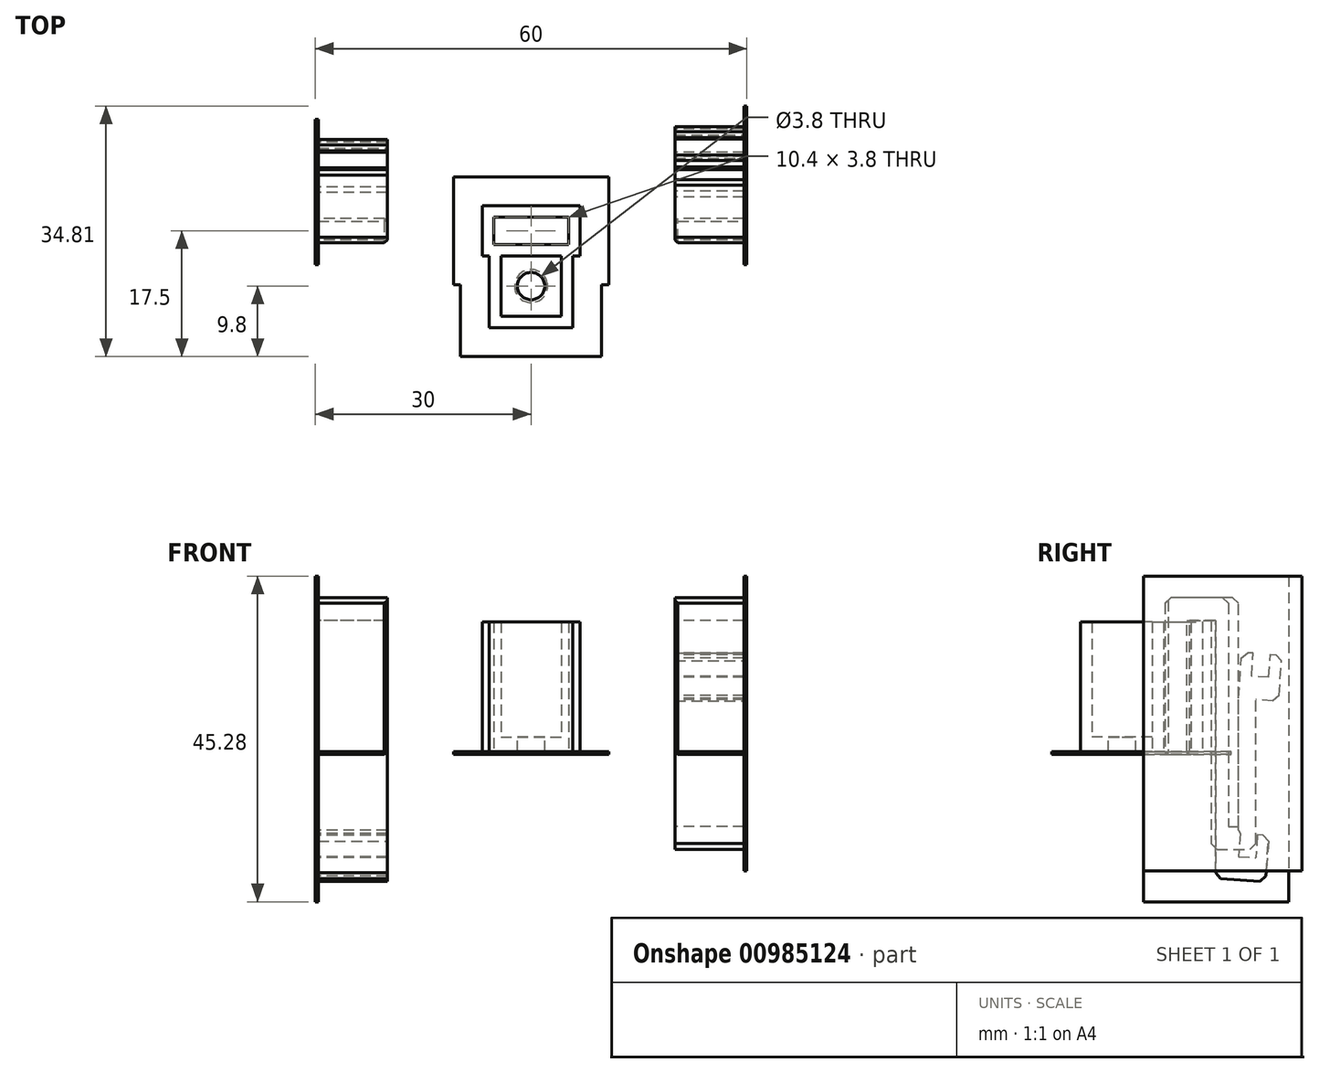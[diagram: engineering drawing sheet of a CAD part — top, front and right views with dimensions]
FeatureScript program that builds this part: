
annotation { "Feature Type Name" : "Feature", "Feature Type Description" : "" }
export const myFeature = defineFeature(function(context is Context, id is Id, definition is map)
    precondition{}
    {
        {
            var Q0;
            Q0=qCreatedBy(makeId("Top.planeOp"),FACE);
            var sketch = newSketch(context, id + "F0", { "sketchPlane" : qUnion([Q0])});
            skLineSegment(sketch, "E0.bottom", {"start": v(-4.2, 4.2) * mm, "end": v(4.2, 4.2) * mm});
            skLineSegment(sketch, "E0.top", {"start": v(-4.2, -4.2) * mm, "end": v(4.2, -4.2) * mm});
            skLineSegment(sketch, "E0.left", {"start": v(-4.2, 4.2) * mm, "end": v(-4.2, -4.2) * mm});
            skLineSegment(sketch, "E0.right", {"start": v(4.2, 4.2) * mm, "end": v(4.2, -4.2) * mm});
            skPoint(sketch, "E0.middle", {"position": v(0, 0) * mm});
            skLineSegment(sketch, "E1.bottom", {"start": v(-5.8, 5.8) * mm, "end": v(5.8, 5.8) * mm});
            skLineSegment(sketch, "E1.top", {"start": v(-5.8, -5.8) * mm, "end": v(5.8, -5.8) * mm});
            skLineSegment(sketch, "E1.left", {"start": v(-5.8, 5.8) * mm, "end": v(-5.8, -5.8) * mm});
            skLineSegment(sketch, "E1.right", {"start": v(5.8, 5.8) * mm, "end": v(5.8, -5.8) * mm});
            skCircle(sketch, "E2", {"center": v(0, 0) * mm, "radius": 1.9 * mm});
            skPoint(sketch, "E3.middle", {"position": v(0, 4.63) * mm});
            skLineSegment(sketch, "E4.bottom", {"start": v(-5.2, 5.8) * mm, "end": v(5.2, 5.8) * mm});
            skLineSegment(sketch, "E4.top", {"start": v(-5.2, 9.6) * mm, "end": v(5.2, 9.6) * mm});
            skLineSegment(sketch, "E4.left", {"start": v(-5.2, 5.8) * mm, "end": v(-5.2, 9.6) * mm});
            skLineSegment(sketch, "E4.right", {"start": v(5.2, 5.8) * mm, "end": v(5.2, 9.6) * mm});
            skPoint(sketch, "E4.middle", {"position": v(0, 7.7) * mm});
            skLineSegment(sketch, "E5.bottom", {"start": v(-6.8, 4.2) * mm, "end": v(6.8, 4.2) * mm});
            skLineSegment(sketch, "E5.top", {"start": v(-6.8, 11.2) * mm, "end": v(6.8, 11.2) * mm});
            skLineSegment(sketch, "E5.left", {"start": v(-6.8, 4.2) * mm, "end": v(-6.8, 11.2) * mm});
            skLineSegment(sketch, "E5.right", {"start": v(6.8, 4.2) * mm, "end": v(6.8, 11.2) * mm});
            skSolve(sketch);
        }
        {
            var Q0;
            Q0=makeQuery(id+"F0.imprint","IMPRINT",FACE,{"disambiguationData":[TD([[makeQuery(id+"F0.imprint","IMPRINT",EDGE,{"derivedFrom":sQuery(id+"F0.wireOp",EDGE,"E0.bottom")}),1.0]])]});
            var Q1;
            Q1=makeQuery(id+"F0.imprint","IMPRINT",FACE,{"disambiguationData":[TD([[makeQuery(id+"F0.imprint","IMPRINT",EDGE,{"derivedFrom":sQuery(id+"F0.wireOp",EDGE,"E0.top")}),-1.0]])]});
            var Q2;
            {var subQ9=sQuery(id+"F0.wireOp",EDGE,"E4.bottom");Q2=makeQuery(id+"F0.imprint","IMPRINT",FACE,{"disambiguationData":[TD([[makeQuery(id+"F0.imprint","IMPRINT",EDGE,{"derivedFrom":subQ9}),-1.0]])]});}
            var Q3;
            Q3=makeQuery(id+"F0.imprint","IMPRINT",FACE,{"disambiguationData":[TD([[makeQuery(id+"F0.imprint","IMPRINT",EDGE,{"derivedFrom":sQuery(id+"F0.wireOp",EDGE,"E4.top")}),1.0]])]});
            var Q4;
            {var subQ0=sQuery(id+"F0.wireOp",EDGE,"E4.bottom");var subQ1=sQuery(id+"F0.wireOp",EDGE,"E1.left");var subQ2=makeQuery(id+"F0.imprint","INTERSECT",VERTEX,{"derivedFrom":[subQ1,subQ0]});Q4=makeQuery(id+"F0.imprint","IMPRINT",FACE,{"disambiguationData":[TD([[makeQuery(id+"F0.imprint","IMPRINT",EDGE,{"disambiguationData":[TD([[subQ2,-1.0]])],"derivedFrom":subQ1}),1.0]])]});}
            extrude(context, id + "F1", {"entities" : qUnion([Q0, Q1, Q2, Q3, Q4]), "depth" : 16 * mm, "offsetDistance" : 25 * mm});
        }
        {
            var Q0;
            Q0=makeQuery(id+"F0.imprint","IMPRINT",FACE,{"disambiguationData":[TD([[makeQuery(id+"F0.imprint","IMPRINT",EDGE,{"derivedFrom":sQuery(id+"F0.wireOp",EDGE,"AogjtpNg-7Dl6-KLo7-kLo7-PgsWRjaplvz6.bottom")}),1.0]])]});
            var Q1;
            Q1=makeQuery(id+"F0.imprint","IMPRINT",FACE,{"disambiguationData":[TD([[makeQuery(id+"F0.imprint","IMPRINT",EDGE,{"derivedFrom":sQuery(id+"F0.wireOp",EDGE,"E0.bottom")}),1.0]])]});
            var Q2;
            Q2=makeQuery(id+"F0.imprint","IMPRINT",FACE,{"disambiguationData":[TD([[makeQuery(id+"F0.imprint","IMPRINT",EDGE,{"derivedFrom":sQuery(id+"F0.wireOp",EDGE,"E0.bottom")}),-1.0]])]});
            var Q3;
            Q3=makeQuery(id+"F0.imprint","IMPRINT",FACE,{"disambiguationData":[TD([[makeQuery(id+"F0.imprint","IMPRINT",EDGE,{"derivedFrom":sQuery(id+"F0.wireOp",EDGE,"lpZYiEbC-BTsA-Mxmd-cXDk-FG9kW4EGSvv5.bottom")}),-1.0]])]});
            var Q4;
            Q4=makeQuery(id+"F0.imprint","IMPRINT",FACE,{"disambiguationData":[TD([[makeQuery(id+"F0.imprint","IMPRINT",EDGE,{"derivedFrom":sQuery(id+"F0.wireOp",EDGE,"fRjwv1VZ-xKsu-zfrT-GSA2-1ylmCSNZtOP4.bottom")}),1.0]])]});
            var Q5;
            {var subQ9=sQuery(id+"F0.wireOp",EDGE,"AogjtpNg-7Dl6-KLo7-kLo7-PgsWRjaplvz6.top");Q5=makeQuery(id+"F0.imprint","IMPRINT",FACE,{"disambiguationData":[TD([[makeQuery(id+"F0.imprint","IMPRINT",EDGE,{"derivedFrom":subQ9}),-1.0]])]});}
            var Q6;
            Q6=makeQuery(id+"F0.imprint","IMPRINT",FACE,{"disambiguationData":[TD([[makeQuery(id+"F0.imprint","IMPRINT",EDGE,{"derivedFrom":sQuery(id+"F0.wireOp",EDGE,"E4.top")}),1.0]])]});
            var Q7;
            Q7=makeQuery(id+"F0.imprint","IMPRINT",FACE,{"disambiguationData":[TD([[makeQuery(id+"F0.imprint","IMPRINT",EDGE,{"derivedFrom":sQuery(id+"F0.wireOp",EDGE,"E0.top")}),-1.0]])]});
            var Q8;
            {var subQ9=sQuery(id+"F0.wireOp",EDGE,"E4.bottom");Q8=makeQuery(id+"F0.imprint","IMPRINT",FACE,{"disambiguationData":[TD([[makeQuery(id+"F0.imprint","IMPRINT",EDGE,{"derivedFrom":subQ9}),-1.0]])]});}
            var Q9;
            Q9=makeQuery(id+"F0.imprint","IMPRINT",FACE,{"disambiguationData":[TD([[makeQuery(id+"F0.imprint","IMPRINT",EDGE,{"derivedFrom":sQuery(id+"F0.wireOp",EDGE,"E0.top")}),1.0]])]});
            var Q10;
            {var subQ0=sQuery(id+"F0.wireOp",EDGE,"E4.bottom");var subQ1=sQuery(id+"F0.wireOp",EDGE,"E1.left");var subQ2=makeQuery(id+"F0.imprint","INTERSECT",VERTEX,{"derivedFrom":[subQ1,subQ0]});Q10=makeQuery(id+"F0.imprint","IMPRINT",FACE,{"disambiguationData":[TD([[makeQuery(id+"F0.imprint","IMPRINT",EDGE,{"disambiguationData":[TD([[subQ2,-1.0]])],"derivedFrom":subQ1}),1.0]])]});}
            extrude(context, id + "F2", {"entities" : qUnion([Q0, Q1, Q2, Q3, Q4, Q5, Q6, Q7, Q8, Q9, Q10]), "operationType" : NewBodyOperationType.ADD, "oppositeDirection" : true, "depth" : 2.4 * mm, "offsetDistance" : 25 * mm});
        }
        {
            var Q0;
            Q0=qCreatedBy(makeId("Right.planeOp"),FACE);
            cPlane(context, id + "F3", {"entities" : qUnion([Q0]), "cplaneType" : CPlaneType.OFFSET, "offset" : 25 * mm, "oppositeDirection" : true, "width" : 150 * mm, "height" : 150 * mm});
        }
        {
            var Q0;
            Q0=qCreatedBy(id+"F3.planeOp",FACE);
            var sketch = newSketch(context, id + "F4", { "sketchPlane" : qUnion([Q0])});
            skPoint(sketch, "E6.0", {"position": v(9.6, -2.4) * mm});
            skPoint(sketch, "E6.1", {"position": v(5.8, -2.4) * mm});
            skPoint(sketch, "E6.2", {"position": v(9.6, 16) * mm});
            skPoint(sketch, "E6.3", {"position": v(5.8, 16) * mm});
            skLineSegment(sketch, "E7.bottom", {"start": v(9.6, -2.4) * mm, "end": v(5.8, -2.4) * mm, "construction": true});
            skLineSegment(sketch, "E7.top", {"start": v(9.6, 16) * mm, "end": v(5.8, 16) * mm, "construction": true});
            skLineSegment(sketch, "E7.left", {"start": v(9.6, -2.4) * mm, "end": v(9.6, 16) * mm, "construction": true});
            skLineSegment(sketch, "E7.right", {"start": v(5.8, -2.4) * mm, "end": v(5.8, 16) * mm, "construction": true});
            skLineSegment(sketch, "E8.bottom", {"start": v(6, -2.4) * mm, "end": v(9.4, -2.4) * mm});
            skLineSegment(sketch, "E8.top", {"start": v(6, 19.4) * mm, "end": v(9.4, 19.4) * mm});
            skLineSegment(sketch, "E8.left", {"start": v(6, -2.4) * mm, "end": v(6, 19.4) * mm});
            skLineSegment(sketch, "E8.right", {"start": v(9.4, -2.4) * mm, "end": v(9.4, 19.4) * mm});
            skLineSegment(sketch, "E9.bottom", {"start": v(9.4, 19.4) * mm, "end": v(13, 19.4) * mm});
            skLineSegment(sketch, "E9.top", {"start": v(9.4, 16.2) * mm, "end": v(13, 16.2) * mm});
            skLineSegment(sketch, "E9.left", {"start": v(9.4, 19.4) * mm, "end": v(9.4, 16.2) * mm});
            skLineSegment(sketch, "E9.right", {"start": v(13, 19.4) * mm, "end": v(13, 16.2) * mm});
            skLineSegment(sketch, "E10.bottom", {"start": v(13, 19.4) * mm, "end": v(16.2, 19.4) * mm});
            skLineSegment(sketch, "E10.top", {"start": v(13, -16.6) * mm, "end": v(16.2, -16.6) * mm});
            skLineSegment(sketch, "E10.left", {"start": v(13, 19.4) * mm, "end": v(13, -16.6) * mm});
            skLineSegment(sketch, "E10.right", {"start": v(16.2, 19.4) * mm, "end": v(16.2, -16.6) * mm});
            skLineSegment(sketch, "E11.bottom", {"start": v(19.97, -20.07) * mm, "end": v(14.38, -19.68) * mm});
            skLineSegment(sketch, "E11.left", {"start": v(19.97, -20.07) * mm, "end": v(20.41, -13.69) * mm});
            skLineSegment(sketch, "E11.right", {"start": v(14.38, -19.68) * mm, "end": v(14.83, -13.3) * mm});
            skLineSegment(sketch, "E12.bottom", {"start": v(18.6, -16.77) * mm, "end": v(16.2, -16.6) * mm});
            skLineSegment(sketch, "E12.left", {"start": v(18.6, -16.77) * mm, "end": v(18.82, -13.58) * mm});
            skLineSegment(sketch, "E12.right", {"start": v(16.2, -16.6) * mm, "end": v(16.42, -13.4) * mm});
            skLineSegment(sketch, "E13", {"start": v(18.82, -13.58) * mm, "end": v(20.41, -13.69) * mm});
            skLineSegment(sketch, "E14", {"start": v(16.42, -13.4) * mm, "end": v(14.83, -13.3) * mm});
            skLineSegment(sketch, "E15", {"start": v(13, -16.6) * mm, "end": v(14.38, -19.68) * mm});
            skLineSegment(sketch, "E16", {"start": v(16.42, -13.4) * mm, "end": v(16.2, -12.9) * mm});
            skLineSegment(sketch, "E17", {"start": v(13, -16.6) * mm, "end": v(13, -19.58) * mm});
            skLineSegment(sketch, "E18", {"start": v(13, -19.58) * mm, "end": v(14.38, -19.68) * mm});
            skSolve(sketch);
        }
        {
            var Q0;
            Q0=makeQuery(id+"F4.imprint","IMPRINT",FACE,{"disambiguationData":[TD([[makeQuery(id+"F4.imprint","IMPRINT",EDGE,{"derivedFrom":sQuery(id+"F4.wireOp",EDGE,"E8.bottom")}),1.0]])]});
            var Q1;
            {var subQ3=sQuery(id+"F4.wireOp",EDGE,"E10.bottom");Q1=makeQuery(id+"F4.imprint","IMPRINT",FACE,{"disambiguationData":[TD([[makeQuery(id+"F4.imprint","IMPRINT",EDGE,{"derivedFrom":subQ3}),-1.0]])]});}
            var Q2;
            {var subQ0=sQuery(id+"F4.wireOp",EDGE,"E9.bottom");Q2=makeQuery(id+"F4.imprint","IMPRINT",FACE,{"disambiguationData":[TD([[makeQuery(id+"F4.imprint","IMPRINT",EDGE,{"derivedFrom":subQ0}),-1.0]])]});}
            var Q3;
            {var subQ3=sQuery(id+"F4.wireOp",EDGE,"E11.right");var subQ5=sQuery(id+"F4.wireOp",EDGE,"E14");var subQ7=makeQuery(id+"F4.imprint","INTERSECT",VERTEX,{"derivedFrom":[subQ3,subQ5]});Q3=makeQuery(id+"F4.imprint","IMPRINT",FACE,{"disambiguationData":[TD([[makeQuery(id+"F4.imprint","IMPRINT",EDGE,{"disambiguationData":[TD([[subQ7,1.0]])],"derivedFrom":subQ3}),-1.0]])]});}
            var Q4;
            {var subQ1=sQuery(id+"F4.wireOp",EDGE,"E11.bottom");Q4=makeQuery(id+"F4.imprint","IMPRINT",FACE,{"disambiguationData":[TD([[makeQuery(id+"F4.imprint","IMPRINT",EDGE,{"derivedFrom":subQ1}),-1.0]])]});}
            var Q5;
            {var subQ0=sQuery(id+"F4.wireOp",EDGE,"E15");Q5=makeQuery(id+"F4.imprint","IMPRINT",FACE,{"disambiguationData":[TD([[makeQuery(id+"F4.imprint","IMPRINT",EDGE,{"derivedFrom":subQ0}),1.0]])]});}
            var Q6;
            {var subQ0=sQuery(id+"F4.wireOp",EDGE,"E12.right");Q6=makeQuery(id+"F4.imprint","IMPRINT",FACE,{"disambiguationData":[TD([[makeQuery(id+"F4.imprint","IMPRINT",EDGE,{"derivedFrom":subQ0}),1.0]])]});}
            var Q7;
            {var subQ0=sQuery(id+"F4.wireOp",EDGE,"E16");Q7=makeQuery(id+"F4.imprint","IMPRINT",FACE,{"disambiguationData":[TD([[makeQuery(id+"F4.imprint","IMPRINT",EDGE,{"derivedFrom":subQ0}),1.0]])]});}
            var Q8;
            Q8=makeQuery(id+"F4.imprint","IMPRINT",FACE,{"disambiguationData":[TD([[makeQuery(id+"F4.imprint","IMPRINT",EDGE,{"derivedFrom":sQuery(id+"F4.wireOp",EDGE,"E15")}),-1.0]])]});
            extrude(context, id + "F5", {"entities" : qUnion([Q0, Q1, Q2, Q3, Q4, Q5, Q6, Q7, Q8]), "depth" : 10 * mm, "offsetDistance" : 25 * mm, "symmetric" : true});
        }
        {
            var Q0;
            Q0=makeQuery(id+"F5.opExtrude","SWEPT_EDGE",EDGE,{"disambiguationData":[OSD([sQuery(id+"F4.wireOp",EDGE,"E11.bottom"),sQuery(id+"F4.wireOp",EDGE,"E11.left")])]});
            var Q1;
            Q1=makeQuery(id+"F5.opExtrude","SWEPT_EDGE",EDGE,{"disambiguationData":[OSD([sQuery(id+"F4.wireOp",EDGE,"E11.left"),sQuery(id+"F4.wireOp",EDGE,"E13")])]});
            var Q2;
            Q2=makeQuery(id+"F5.opExtrude","SWEPT_EDGE",EDGE,{"disambiguationData":[OSD([sQuery(id+"F4.wireOp",EDGE,"E11.bottom"),sQuery(id+"F4.wireOp",EDGE,"E11.right"),sQuery(id+"F4.wireOp",EDGE,"E15")])]});
            var Q3;
            Q3=makeQuery(id+"F5.opExtrude","SWEPT_EDGE",EDGE,{"disambiguationData":[OSD([sQuery(id+"F4.wireOp",EDGE,"E10.bottom"),sQuery(id+"F4.wireOp",EDGE,"E10.right")])]});
            var Q4;
            Q4=makeQuery(id+"F5.opExtrude","SWEPT_EDGE",EDGE,{"disambiguationData":[OSD([sQuery(id+"F4.wireOp",EDGE,"E8.top"),sQuery(id+"F4.wireOp",EDGE,"E8.left")])]});
            var Q5;
            Q5=makeQuery(id+"F5.opExtrude","SWEPT_EDGE",EDGE,{"disambiguationData":[OSD([sQuery(id+"F4.wireOp",EDGE,"E17"),sQuery(id+"F4.wireOp",EDGE,"E18")])]});
            chamfer(context, id + "F6", {"entities" : qUnion([Q0, Q1, Q2, Q3, Q4, Q5]), "width" : 0.8 * mm, "tangentPropagation" : true});
        }
        {
            var Q0;
            Q0=qCreatedBy(makeId("Right.planeOp"),FACE);
            cPlane(context, id + "F7", {"entities" : qUnion([Q0]), "cplaneType" : CPlaneType.OFFSET, "offset" : 25 * mm, "width" : 150 * mm, "height" : 150 * mm});
        }
        {
            var Q0;
            Q0=qCreatedBy(id+"F7.planeOp",FACE);
            var sketch = newSketch(context, id + "F8", { "sketchPlane" : qUnion([Q0])});
            skPoint(sketch, "E19.0", {"position": v(9.6, -2.4) * mm});
            skPoint(sketch, "E19.1", {"position": v(5.8, -2.4) * mm});
            skPoint(sketch, "E19.2", {"position": v(5.8, 16) * mm});
            skPoint(sketch, "E19.3", {"position": v(9.6, 16) * mm});
            skLineSegment(sketch, "E20.bottom", {"start": v(5.8, 16) * mm, "end": v(9.6, 16) * mm, "construction": true});
            skLineSegment(sketch, "E20.top", {"start": v(5.8, -2.4) * mm, "end": v(9.6, -2.4) * mm, "construction": true});
            skLineSegment(sketch, "E20.left", {"start": v(5.8, 16) * mm, "end": v(5.8, -2.4) * mm, "construction": true});
            skLineSegment(sketch, "E20.right", {"start": v(9.6, 16) * mm, "end": v(9.6, -2.4) * mm, "construction": true});
            skPoint(sketch, "E21.0", {"position": v(9.4, 19.4) * mm});
            skPoint(sketch, "E21.1", {"position": v(6, 19.4) * mm});
            skPoint(sketch, "E21.2", {"position": v(9.4, -2.4) * mm});
            skPoint(sketch, "E21.3", {"position": v(6, -2.4) * mm});
            skLineSegment(sketch, "E22.bottom", {"start": v(9.4, 19.4) * mm, "end": v(6, 19.4) * mm});
            skLineSegment(sketch, "E22.top", {"start": v(9.4, -2.4) * mm, "end": v(6, -2.4) * mm});
            skLineSegment(sketch, "E22.left", {"start": v(9.4, 19.4) * mm, "end": v(9.4, -2.4) * mm});
            skLineSegment(sketch, "E22.right", {"start": v(6, 19.4) * mm, "end": v(6, -2.4) * mm});
            skPoint(sketch, "E23.0", {"position": v(9.4, 16.2) * mm});
            skLineSegment(sketch, "E24.bottom", {"start": v(9.4, 19.4) * mm, "end": v(9.4, 19.4) * mm});
            skLineSegment(sketch, "E24.top", {"start": v(9.4, 16.2) * mm, "end": v(9.4, 16.2) * mm});
            skLineSegment(sketch, "E24.left", {"start": v(9.4, 19.4) * mm, "end": v(9.4, 16.2) * mm});
            skLineSegment(sketch, "E24.right", {"start": v(9.4, 19.4) * mm, "end": v(9.4, 16.2) * mm});
            skLineSegment(sketch, "E25.bottom", {"start": v(9.4, 19.4) * mm, "end": v(12.4, 19.4) * mm});
            skLineSegment(sketch, "E25.top", {"start": v(9.4, 16.2) * mm, "end": v(12.4, 16.2) * mm});
            skLineSegment(sketch, "E25.right", {"start": v(12.4, 19.4) * mm, "end": v(12.4, 16.2) * mm});
            skLineSegment(sketch, "E26.0", {"start": v(16.2, 5.4) * mm, "end": v(16.65, 11.78) * mm});
            skLineSegment(sketch, "E26.1", {"start": v(18.02, 8.48) * mm, "end": v(18.24, 11.67) * mm});
            skLineSegment(sketch, "E26.2", {"start": v(20.41, 8.31) * mm, "end": v(20.64, 11.5) * mm});
            skLineSegment(sketch, "E26.3", {"start": v(21.79, 5) * mm, "end": v(22.23, 11.4) * mm});
            skLineSegment(sketch, "E26.4", {"start": v(20.64, 11.5) * mm, "end": v(22.23, 11.4) * mm});
            skLineSegment(sketch, "E26.5", {"start": v(21.79, 5) * mm, "end": v(16.2, 5.4) * mm});
            skLineSegment(sketch, "E26.6", {"start": v(18.24, 11.67) * mm, "end": v(16.65, 11.78) * mm});
            skLineSegment(sketch, "E26.7", {"start": v(20.41, 8.31) * mm, "end": v(18.02, 8.48) * mm});
            skLineSegment(sketch, "E27.bottom", {"start": v(12.4, 19.4) * mm, "end": v(14.8, 19.4) * mm});
            skLineSegment(sketch, "E27.top", {"start": v(12.4, -15.6) * mm, "end": v(14.8, -15.6) * mm});
            skLineSegment(sketch, "E27.left", {"start": v(12.4, 19.4) * mm, "end": v(12.4, -15.6) * mm});
            skLineSegment(sketch, "E27.right", {"start": v(14.8, 19.4) * mm, "end": v(14.8, -15.6) * mm});
            skLineSegment(sketch, "E28.bottom", {"start": v(14.8, -15.6) * mm, "end": v(16.2, -15.6) * mm});
            skLineSegment(sketch, "E28.top", {"start": v(14.8, -12.4) * mm, "end": v(16.2, -12.4) * mm});
            skLineSegment(sketch, "E28.left", {"start": v(14.8, -15.6) * mm, "end": v(14.8, -12.4) * mm});
            skLineSegment(sketch, "E28.right", {"start": v(16.2, -15.6) * mm, "end": v(16.2, -12.4) * mm});
            skLineSegment(sketch, "E29.bottom", {"start": v(16.2, -15.6) * mm, "end": v(18.6, -15.6) * mm});
            skLineSegment(sketch, "E29.top", {"start": v(16.2, 5.4) * mm, "end": v(18.6, 5.4) * mm});
            skLineSegment(sketch, "E29.left", {"start": v(16.2, -15.6) * mm, "end": v(16.2, 5.4) * mm});
            skLineSegment(sketch, "E29.right", {"start": v(18.6, -15.6) * mm, "end": v(18.6, 5.4) * mm});
            skSolve(sketch);
        }
        {
            var Q0;
            Q0=qSketchRegion(id+"F8",true);
            extrude(context, id + "F9", {"entities" : qUnion([Q0]), "depth" : 10 * mm, "offsetDistance" : 25 * mm, "symmetric" : true});
        }
        {
            var Q0;
            Q0=makeQuery(id+"F9.opExtrude","SWEPT_EDGE",EDGE,{"disambiguationData":[OSD([sQuery(id+"F8.wireOp",EDGE,"E26.3"),sQuery(id+"F8.wireOp",EDGE,"E26.4")])]});
            var Q1;
            Q1=makeQuery(id+"F9.opExtrude","SWEPT_EDGE",EDGE,{"disambiguationData":[OSD([sQuery(id+"F8.wireOp",EDGE,"E26.3"),sQuery(id+"F8.wireOp",EDGE,"E26.5")])]});
            var Q2;
            Q2=makeQuery(id+"F9.opExtrude","SWEPT_EDGE",EDGE,{"disambiguationData":[OSD([sQuery(id+"F8.wireOp",EDGE,"gtvTyELX-qYsY-zlD4-YZin-kNKeZDM44uR5.bottom"),sQuery(id+"F8.wireOp",EDGE,"gtvTyELX-qYsY-zlD4-YZin-kNKeZDM44uR5.right")])]});
            var Q3;
            Q3=makeQuery(id+"F9.opExtrude","SWEPT_EDGE",EDGE,{"disambiguationData":[OSD([sQuery(id+"F8.wireOp",EDGE,"pzn4xJtv-Sc2h-J7Oc-zair-ZdfKoGXIpqRY.top"),sQuery(id+"F8.wireOp",EDGE,"pzn4xJtv-Sc2h-J7Oc-zair-ZdfKoGXIpqRY.left")])]});
            var Q4;
            Q4=makeQuery(id+"F9.opExtrude","SWEPT_EDGE",EDGE,{"disambiguationData":[OSD([sQuery(id+"F8.wireOp",EDGE,"E26.0"),sQuery(id+"F8.wireOp",EDGE,"E26.6"),sQuery(id+"F8.wireOp",EDGE,"qTeprqho-zbRK-rMkQ-vlma-PGJ56aoAsNja")])]});
            var Q5;
            Q5=makeQuery(id+"F9.opExtrude","SWEPT_EDGE",EDGE,{"disambiguationData":[OSD([sQuery(id+"F8.wireOp",EDGE,"pzn4xJtv-Sc2h-J7Oc-zair-ZdfKoGXIpqRY.bottom"),sQuery(id+"F8.wireOp",EDGE,"pzn4xJtv-Sc2h-J7Oc-zair-ZdfKoGXIpqRY.right")])]});
            var Q6;
            Q6=makeQuery(id+"F9.opExtrude","SWEPT_EDGE",EDGE,{"disambiguationData":[OSD([sQuery(id+"F8.wireOp",EDGE,"E22.bottom"),sQuery(id+"F8.wireOp",EDGE,"E22.right")])]});
            var Q7;
            Q7=makeQuery(id+"F9.opExtrude","SWEPT_EDGE",EDGE,{"disambiguationData":[OSD([sQuery(id+"F8.wireOp",EDGE,"E27.bottom"),sQuery(id+"F8.wireOp",EDGE,"E27.right")])]});
            var Q8;
            Q8=makeQuery(id+"F9.opExtrude","SWEPT_EDGE",EDGE,{"disambiguationData":[OSD([sQuery(id+"F8.wireOp",EDGE,"E29.bottom"),sQuery(id+"F8.wireOp",EDGE,"E29.right")])]});
            var Q9;
            Q9=makeQuery(id+"F9.opExtrude","SWEPT_EDGE",EDGE,{"disambiguationData":[OSD([sQuery(id+"F8.wireOp",EDGE,"E27.top"),sQuery(id+"F8.wireOp",EDGE,"E27.left")])]});
            chamfer(context, id + "F10", {"entities" : qUnion([Q0, Q1, Q2, Q3, Q4, Q5, Q6, Q7, Q8, Q9]), "width" : 0.8 * mm, "tangentPropagation" : true});
        }
        {
            var Q0;
            Q0=makeQuery(id+"F2.opExtrude","CAP_FACE",FACE,{"disambiguationData":[OSD([sQuery(id+"F0.wireOp",EDGE,"E1.top"),sQuery(id+"F0.wireOp",EDGE,"E1.left"),sQuery(id+"F0.wireOp",EDGE,"E1.right"),sQuery(id+"F0.wireOp",EDGE,"E2"),sQuery(id+"F0.wireOp",EDGE,"E4.bottom"),sQuery(id+"F0.wireOp",EDGE,"E4.top"),sQuery(id+"F0.wireOp",EDGE,"E4.left"),sQuery(id+"F0.wireOp",EDGE,"E4.right"),sQuery(id+"F0.wireOp",EDGE,"E5.bottom"),sQuery(id+"F0.wireOp",EDGE,"E5.top"),sQuery(id+"F0.wireOp",EDGE,"E5.left"),sQuery(id+"F0.wireOp",EDGE,"E5.right")])],"isStart":false});
            var sketch = newSketch(context, id + "F11", { "sketchPlane" : qUnion([Q0])});
            skSolve(sketch);
        }
        {
            var Q0;
            Q0=makeQuery(id+"F9.opExtrude","CAP_EDGE",EDGE,{"disambiguationData":[OSD([sQuery(id+"F8.wireOp",EDGE,"E22.right")])],"isStart":false});
            var Q1;
            Q1=makeQuery(id+"F9.opExtrude","CAP_EDGE",EDGE,{"disambiguationData":[OSD([sQuery(id+"F8.wireOp",EDGE,"E22.left")])],"isStart":false});
            var Q2;
            Q2=makeQuery(id+"F9.opExtrude","CAP_EDGE",EDGE,{"disambiguationData":[OSD([sQuery(id+"F8.wireOp",EDGE,"E22.right")])],"isStart":true});
            var Q3;
            Q3=makeQuery(id+"F9.opExtrude","SWEPT_EDGE",EDGE,{"disambiguationData":[OSD([sQuery(id+"F8.wireOp",EDGE,"E22.top"),sQuery(id+"F8.wireOp",EDGE,"E22.right")])]});
            var Q4;
            Q4=makeQuery(id+"F9.opExtrude","CAP_EDGE",EDGE,{"disambiguationData":[OSD([sQuery(id+"F8.wireOp",EDGE,"E22.top")])],"isStart":true});
            var Q5;
            Q5=makeQuery(id+"F9.opExtrude","SWEPT_EDGE",EDGE,{"disambiguationData":[OSD([sQuery(id+"F8.wireOp",EDGE,"E22.top"),sQuery(id+"F8.wireOp",EDGE,"E22.left")])]});
            var Q6;
            Q6=makeQuery(id+"F9.opExtrude","CAP_EDGE",EDGE,{"disambiguationData":[OSD([sQuery(id+"F8.wireOp",EDGE,"E22.top")])],"isStart":false});
            var Q7;
            Q7=makeQuery(id+"F9.opExtrude","CAP_EDGE",EDGE,{"disambiguationData":[OSD([sQuery(id+"F8.wireOp",EDGE,"E22.left")])],"isStart":true});
            var Q8;
            Q8=makeQuery(id+"F5.opExtrude","CAP_EDGE",EDGE,{"disambiguationData":[OSD([sQuery(id+"F4.wireOp",EDGE,"E8.bottom")])],"isStart":true});
            var Q9;
            Q9=makeQuery(id+"F5.opExtrude","SWEPT_EDGE",EDGE,{"disambiguationData":[OSD([sQuery(id+"F4.wireOp",EDGE,"E8.bottom"),sQuery(id+"F4.wireOp",EDGE,"E8.left")])]});
            var Q10;
            Q10=makeQuery(id+"F5.opExtrude","CAP_EDGE",EDGE,{"disambiguationData":[OSD([sQuery(id+"F4.wireOp",EDGE,"E8.bottom")])],"isStart":false});
            var Q11;
            Q11=makeQuery(id+"F5.opExtrude","SWEPT_EDGE",EDGE,{"disambiguationData":[OSD([sQuery(id+"F4.wireOp",EDGE,"E8.bottom"),sQuery(id+"F4.wireOp",EDGE,"E8.right")])]});
            var Q12;
            Q12=makeQuery(id+"F5.opExtrude","CAP_EDGE",EDGE,{"disambiguationData":[OSD([sQuery(id+"F4.wireOp",EDGE,"E8.right")])],"isStart":true});
            var Q13;
            Q13=makeQuery(id+"F5.opExtrude","CAP_EDGE",EDGE,{"disambiguationData":[OSD([sQuery(id+"F4.wireOp",EDGE,"E8.left")])],"isStart":true});
            var Q14;
            Q14=makeQuery(id+"F5.opExtrude","CAP_EDGE",EDGE,{"disambiguationData":[OSD([sQuery(id+"F4.wireOp",EDGE,"E8.right")])],"isStart":false});
            var Q15;
            Q15=makeQuery(id+"F5.opExtrude","CAP_EDGE",EDGE,{"disambiguationData":[OSD([sQuery(id+"F4.wireOp",EDGE,"E8.left")])],"isStart":false});
            chamfer(context, id + "F12", {"entities" : qUnion([Q0, Q1, Q2, Q3, Q4, Q5, Q6, Q7, Q8, Q9, Q10, Q11, Q12, Q13, Q14, Q15]), "width" : 0.4 * mm, "tangentPropagation" : true});
        }
        {
            var Q0;
            Q0=makeQuery(id+"F2.opExtrude","CAP_EDGE",EDGE,{"disambiguationData":[OSD([sQuery(id+"F0.wireOp",EDGE,"E2")])],"isStart":false});
            chamfer(context, id + "F13", {"entities" : qUnion([Q0]), "width" : 0.4 * mm, "tangentPropagation" : true});
        }
        {
            var Q0;
            Q0=qCreatedBy(makeId("Front.planeOp"),FACE);
            var sketch = newSketch(context, id + "F14", { "sketchPlane" : qUnion([Q0])});
            skPoint(sketch, "E30.0", {"position": v(-5.8, -2.4) * mm});
            skLineSegment(sketch, "E31.bottom", {"start": v(-5.8, -2.4) * mm, "end": v(-9.8, -2.4) * mm});
            skLineSegment(sketch, "E31.top", {"start": v(-5.8, -2) * mm, "end": v(-9.8, -2) * mm});
            skLineSegment(sketch, "E31.left", {"start": v(-5.8, -2.4) * mm, "end": v(-5.8, -2) * mm});
            skLineSegment(sketch, "E31.right", {"start": v(-9.8, -2.4) * mm, "end": v(-9.8, -2) * mm});
            skSolve(sketch);
        }
        {
            var Q0;
            Q0=makeQuery(id+"F14.imprint","IMPRINT",FACE,{"disambiguationData":[TD([[makeQuery(id+"F14.imprint","IMPRINT",EDGE,{"derivedFrom":sQuery(id+"F14.wireOp",EDGE,"E31.bottom")}),-1.0]])]});
            var Q1;
            Q1=makeQuery(id+"F2.opExtrude","CAP_EDGE",EDGE,{"disambiguationData":[OSD([sQuery(id+"F0.wireOp",EDGE,"E1.left")])],"isStart":false});
            var Q2;
            Q2=makeQuery(id+"F2.opExtrude","CAP_EDGE",EDGE,{"disambiguationData":[OSD([sQuery(id+"F0.wireOp",EDGE,"E1.top")])],"isStart":false});
            var Q3;
            Q3=makeQuery(id+"F2.opExtrude","CAP_EDGE",EDGE,{"disambiguationData":[OSD([sQuery(id+"F0.wireOp",EDGE,"E1.right")])],"isStart":false});
            var Q4;
            Q4=makeQuery(id+"F2.opExtrude","CAP_EDGE",EDGE,{"disambiguationData":[OSD([sQuery(id+"F0.wireOp",EDGE,"E5.right")])],"isStart":false});
            var Q5;
            {var subQ0=sQuery(id+"F0.wireOp",EDGE,"E5.bottom");Q5=makeQuery(id+"F2.opExtrude","CAP_EDGE",EDGE,{"disambiguationData":[OSD([subQ0]),TDD([makeQuery(id+"F0.imprint","IMPRINT",EDGE,{"disambiguationData":[TD([[makeQuery(id+"F0.imprint","INTERSECT",VERTEX,{"derivedFrom":[subQ0,sQuery(id+"F0.wireOp",EDGE,"E5.right")]}),1.0]])],"derivedFrom":subQ0})])],"isStart":false});}
            var Q6;
            {var subQ0=sQuery(id+"F0.wireOp",EDGE,"E5.bottom");Q6=makeQuery(id+"F2.opExtrude","CAP_EDGE",EDGE,{"disambiguationData":[OSD([subQ0]),TDD([makeQuery(id+"F0.imprint","IMPRINT",EDGE,{"disambiguationData":[TD([[makeQuery(id+"F0.imprint","INTERSECT",VERTEX,{"derivedFrom":[subQ0,sQuery(id+"F0.wireOp",EDGE,"E5.left")]}),-1.0]])],"derivedFrom":subQ0})])],"isStart":false});}
            var Q7;
            Q7=makeQuery(id+"F2.opExtrude","CAP_EDGE",EDGE,{"disambiguationData":[OSD([sQuery(id+"F0.wireOp",EDGE,"E5.left")])],"isStart":false});
            var Q8;
            Q8=makeQuery(id+"F2.opExtrude","CAP_EDGE",EDGE,{"disambiguationData":[OSD([sQuery(id+"F0.wireOp",EDGE,"E5.top")])],"isStart":false});
            sweep(context, id + "F15", {"operationType" : NewBodyOperationType.ADD, "profiles" : qUnion([Q0]), "path" : qUnion([Q1, Q2, Q3, Q4, Q5, Q6, Q7, Q8])});
        }
        {
            var Q0;
            Q0=makeQuery(id+"F5.opExtrude","CAP_FACE",FACE,{"disambiguationData":[OSD([sQuery(id+"F4.wireOp",EDGE,"E8.bottom"),sQuery(id+"F4.wireOp",EDGE,"E8.top"),sQuery(id+"F4.wireOp",EDGE,"E8.left"),sQuery(id+"F4.wireOp",EDGE,"E8.right"),sQuery(id+"F4.wireOp",EDGE,"E9.bottom"),sQuery(id+"F4.wireOp",EDGE,"E9.top"),sQuery(id+"F4.wireOp",EDGE,"E10.bottom"),sQuery(id+"F4.wireOp",EDGE,"E10.left"),sQuery(id+"F4.wireOp",EDGE,"E10.right"),sQuery(id+"F4.wireOp",EDGE,"E11.bottom"),sQuery(id+"F4.wireOp",EDGE,"E11.left"),sQuery(id+"F4.wireOp",EDGE,"E12.bottom"),sQuery(id+"F4.wireOp",EDGE,"E12.left"),sQuery(id+"F4.wireOp",EDGE,"E12.right"),sQuery(id+"F4.wireOp",EDGE,"E13"),sQuery(id+"F4.wireOp",EDGE,"E15"),sQuery(id+"F4.wireOp",EDGE,"E16")])],"isStart":true});
            var sketch = newSketch(context, id + "F16", { "sketchPlane" : qUnion([Q0])});
            skLineSegment(sketch, "E32.bottom", {"start": v(-3, 22.4) * mm, "end": v(-23.2, 22.4) * mm});
            skLineSegment(sketch, "E32.top", {"start": v(-3, -22.88) * mm, "end": v(-23.2, -22.88) * mm});
            skLineSegment(sketch, "E32.left", {"start": v(-3, 22.4) * mm, "end": v(-3, -22.88) * mm});
            skLineSegment(sketch, "E32.right", {"start": v(-23.2, 22.4) * mm, "end": v(-23.2, -22.88) * mm});
            skSolve(sketch);
        }
        {
            var Q0;
            Q0=qSketchRegion(id+"F16",true);
            extrude(context, id + "F17", {"entities" : qUnion([Q0]), "operationType" : NewBodyOperationType.ADD, "oppositeDirection" : true, "depth" : 0.4 * mm, "offsetDistance" : 25 * mm});
        }
        {
            var Q0;
            Q0=makeQuery(id+"F9.opExtrude","CAP_FACE",FACE,{"disambiguationData":[OSD([sQuery(id+"F8.wireOp",EDGE,"E22.bottom"),sQuery(id+"F8.wireOp",EDGE,"E22.top"),sQuery(id+"F8.wireOp",EDGE,"E22.left"),sQuery(id+"F8.wireOp",EDGE,"E22.right"),sQuery(id+"F8.wireOp",EDGE,"E25.bottom"),sQuery(id+"F8.wireOp",EDGE,"E25.top"),sQuery(id+"F8.wireOp",EDGE,"E26.1"),sQuery(id+"F8.wireOp",EDGE,"E26.2"),sQuery(id+"F8.wireOp",EDGE,"E26.3"),sQuery(id+"F8.wireOp",EDGE,"E26.4"),sQuery(id+"F8.wireOp",EDGE,"E26.5"),sQuery(id+"F8.wireOp",EDGE,"E26.7"),sQuery(id+"F8.wireOp",EDGE,"pzn4xJtv-Sc2h-J7Oc-zair-ZdfKoGXIpqRY.bottom"),sQuery(id+"F8.wireOp",EDGE,"pzn4xJtv-Sc2h-J7Oc-zair-ZdfKoGXIpqRY.left"),sQuery(id+"F8.wireOp",EDGE,"vUsKkYh5-iqO0-ygEX-7fbj-hNIgQPiPXa8G.left"),sQuery(id+"F8.wireOp",EDGE,"79FwRNYW-v71M-SnH2-85o6-K5286zw6z0ES"),sQuery(id+"F8.wireOp",EDGE,"QHimpM6D-nGDS-kpgz-XPSz-bpLJxk910mxU")])],"isStart":false});
            var sketch = newSketch(context, id + "F18", { "sketchPlane" : qUnion([Q0])});
            skLineSegment(sketch, "E33.bottom", {"start": v(3, 22.4) * mm, "end": v(25, 22.4) * mm});
            skLineSegment(sketch, "E33.top", {"start": v(3, -18.6) * mm, "end": v(25, -18.6) * mm});
            skLineSegment(sketch, "E33.left", {"start": v(3, 22.4) * mm, "end": v(3, -18.6) * mm});
            skLineSegment(sketch, "E33.right", {"start": v(25, 22.4) * mm, "end": v(25, -18.6) * mm});
            skSolve(sketch);
        }
        {
            var Q0;
            Q0=qSketchRegion(id+"F18",true);
            extrude(context, id + "F19", {"entities" : qUnion([Q0]), "operationType" : NewBodyOperationType.ADD, "oppositeDirection" : true, "depth" : 0.4 * mm, "offsetDistance" : 25 * mm});
        }
    });
